# Revit family: SHL-L-180-xxx-840-SMx
name_source: partatom
category: Leuchten
revit_build: Autodesk Revit 2017 (Build: 20190508_0315(x64)
units: mm (PartAtom-declared; Revit-internal decimal feet)

## family parameters
Basisbauteil = Fläche
Beim Laden mit Abzugskörper schneiden = Nein
Bemaßung runder Anschluss = Durchmesser verwenden
Gemeinsam genutzt = Nein
Lichtquelle = Ja
OmniClass-Nummer = 23.80.70.11
OmniClass-Titel = Luminaries for Internal Lighting
Raumberechnungspunkt = Nein
Teiletyp = Normal

## types (4) — shared parameters
Baugruppenkennzeichen = D5020200
Datei für fotometrisches Netz = SHL-L 180620-840 SM.IES
Emissionsform beim Rendern sichtbar = Nein
Farbfilter = 16777215
Farbtemperaturverschiebung bei Dämpfen der Lampe = <Keine Auswahl>
Hersteller = RIDI Leuchten GmbH
Lampe = LED
Neigungswinkel = 90.00°
URL = www.ridi.de
Von Breite des Rechtecks ausssenden = 1473 mm  [stored 4.83268 ft]
Von Länge des Rechtecks aussenden = 174 mm  [stored 0.570866 ft]
brand = RIDI
conformity mark = CE
electrical safety class = 1
height = 80 mm
ingress protection (IP) code = IP40
length = 1500 mm
nominal frequency = 50-60Hz
nominal voltage = 230
voltage type (AC, DC, UC) = AC
weight = 11kg
width = 200 mm
zero-valued in all types: Vorgabe-Ansicht

## per-type parameters (varying)
| type | Modell | Scheinlast | rated input power |
| SHL-L 180/620-840 SM | 0650099 | 48 VA | 48 |
| SHL-L 180/620-840 SM-DA | 0660099 | 48 VA | 48 |
| SHL-L 180/935-840 SM | 0650622 | 70 VA | 70 |
| SHL-L 180/935-840 SM-DA | 0660622 | 70 VA | 70 |

note: column(s) folded — value = type name in every type: product name

note: [stored X ft] marks values corroborated as IEEE doubles in the binary element streams (Revit-internal decimal feet)
